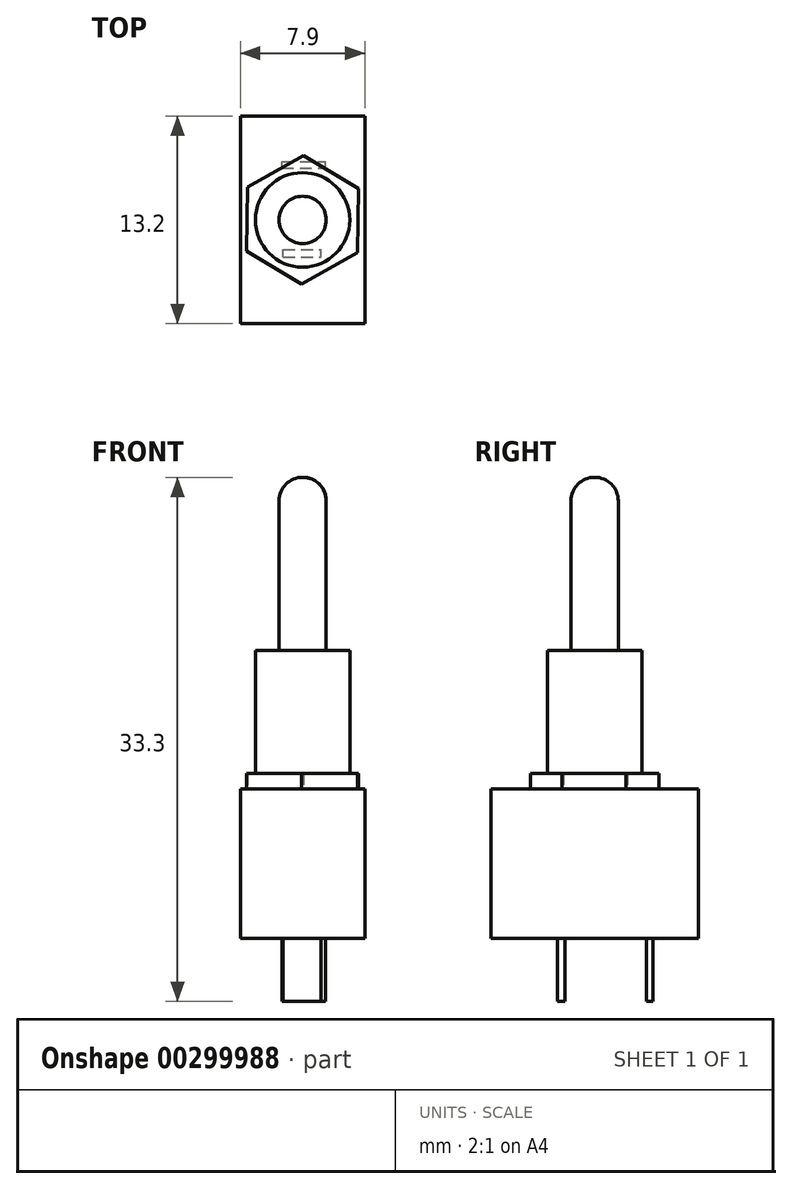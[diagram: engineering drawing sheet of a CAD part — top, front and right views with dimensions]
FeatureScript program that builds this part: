
annotation { "Feature Type Name" : "Feature", "Feature Type Description" : "" }
export const myFeature = defineFeature(function(context is Context, id is Id, definition is map)
    precondition{}
    {
        {
            var Q0;
            Q0=qCreatedBy(makeId("Right.planeOp"),FACE);
            var sketch = newSketch(context, id + "F0", { "sketchPlane" : qUnion([Q0])});
            skLineSegment(sketch, "E0.bottom", {"start": v(0, 0) * mm, "end": v(13.2, 0) * mm});
            skLineSegment(sketch, "E0.top", {"start": v(0, 9.5) * mm, "end": v(13.2, 9.5) * mm});
            skLineSegment(sketch, "E0.left", {"start": v(0, 0) * mm, "end": v(0, 9.5) * mm});
            skLineSegment(sketch, "E0.right", {"start": v(13.2, 0) * mm, "end": v(13.2, 9.5) * mm});
            skSolve(sketch);
        }
        {
            var Q0;
            Q0 = qSketchRegion(id + "F0", true);
            extrude(context, id + "F1", {"entities" : qUnion([Q0]), "depth" : 7.9 * mm});
        }
        {
            var Q0;
            Q0=makeQuery(id+"F1.opExtrude","SWEPT_FACE",FACE,{"disambiguationData":[OSD([sQuery(id+"F0.wireOp",EDGE,"E0.top")])]});
            var sketch = newSketch(context, id + "F2", { "sketchPlane" : qUnion([Q0])});
            skCircle(sketch, "E1", {"center": v(3.95, 6.6) * mm, "radius": 3 * mm});
            skPoint(sketch, "E1.centerSnap0", {"position": v(0, 6.6) * mm});
            skSolve(sketch);
        }
        {
            var Q0;
            Q0 = qSketchRegion(id + "F2", true);
            extrude(context, id + "F3", {"entities" : qUnion([Q0]), "operationType" : NewBodyOperationType.ADD, "depth" : 8.8 * mm});
        }
        {
            var Q0;
            Q0=makeQuery(id+"F3.opExtrude","CAP_FACE",FACE,{"disambiguationData":[OSD([sQuery(id+"F2.wireOp",EDGE,"E1")])],"isStart":false});
            var sketch = newSketch(context, id + "F4", { "sketchPlane" : qUnion([Q0])});
            skCircle(sketch, "E2", {"center": v(3.95, 6.6) * mm, "radius": 1.5 * mm});
            skSolve(sketch);
        }
        {
            var Q0;
            Q0 = qSketchRegion(id + "F4", true);
            extrude(context, id + "F5", {"entities" : qUnion([Q0]), "operationType" : NewBodyOperationType.ADD, "depth" : 11 * mm});
        }
        {
            var Q0;
            Q0=makeQuery(id+"F5.opExtrude","CAP_EDGE",EDGE,{"disambiguationData":[OSD([sQuery(id+"F4.wireOp",EDGE,"E2")])],"isStart":false});
            fillet(context, id + "F6", {"entities" : qUnion([Q0]), "radius" : 1.5 * mm, "tangentPropagation" : true, "allowEdgeOverflow" : false});
        }
        {
            var Q0;
            Q0=makeQuery(id+"F1.opExtrude","SWEPT_FACE",FACE,{"disambiguationData":[OSD([sQuery(id+"F0.wireOp",EDGE,"E0.bottom")])]});
            var sketch = newSketch(context, id + "F7", { "sketchPlane" : qUnion([Q0])});
            skLineSegment(sketch, "E3.bottom", {"start": v(2.7, -4.25) * mm, "end": v(5.13, -4.25) * mm});
            skLineSegment(sketch, "E3.top", {"start": v(2.7, -4.72) * mm, "end": v(5.13, -4.72) * mm});
            skLineSegment(sketch, "E3.left", {"start": v(2.7, -4.25) * mm, "end": v(2.7, -4.72) * mm});
            skLineSegment(sketch, "E3.right", {"start": v(5.13, -4.25) * mm, "end": v(5.13, -4.72) * mm});
            skLineSegment(sketch, "E4.bottom", {"start": v(2.63, -9.9) * mm, "end": v(5.42, -9.9) * mm});
            skLineSegment(sketch, "E4.top", {"start": v(2.63, -10.29) * mm, "end": v(5.42, -10.29) * mm});
            skLineSegment(sketch, "E4.left", {"start": v(2.63, -9.9) * mm, "end": v(2.63, -10.29) * mm});
            skLineSegment(sketch, "E4.right", {"start": v(5.42, -9.9) * mm, "end": v(5.42, -10.29) * mm});
            skSolve(sketch);
        }
        {
            var Q0;
            Q0 = qSketchRegion(id + "F7", true);
            extrude(context, id + "F8", {"entities" : qUnion([Q0]), "operationType" : NewBodyOperationType.ADD, "depth" : 4 * mm});
        }
        {
            var Q0;
            Q0=makeQuery(id+"F1.opExtrude","SWEPT_FACE",FACE,{"disambiguationData":[OSD([sQuery(id+"F0.wireOp",EDGE,"E0.top")])]});
            var sketch = newSketch(context, id + "F9", { "sketchPlane" : qUnion([Q0])});
            skCircle(sketch, "E5.cCircle", {"center": v(3.95, 6.6) * mm, "radius": 3.53 * mm, "construction": true});
            skLineSegment(sketch, "E5.0", {"start": v(7.45, 4.52) * mm, "end": v(3.9, 2.53) * mm});
            skLineSegment(sketch, "E5.1", {"start": v(3.9, 2.53) * mm, "end": v(0.4, 4.6) * mm});
            skLineSegment(sketch, "E5.2", {"start": v(0.4, 4.6) * mm, "end": v(0.45, 8.68) * mm});
            skLineSegment(sketch, "E5.3", {"start": v(0.45, 8.68) * mm, "end": v(4, 10.67) * mm});
            skLineSegment(sketch, "E5.4", {"start": v(4, 10.67) * mm, "end": v(7.5, 8.6) * mm});
            skLineSegment(sketch, "E5.5", {"start": v(7.5, 8.6) * mm, "end": v(7.45, 4.52) * mm});
            skPoint(sketch, "E5.0.midPoint", {"position": v(5.67, 3.52) * mm});
            skSolve(sketch);
        }
        {
            var Q0;
            Q0 = qSketchRegion(id + "F9", true);
            extrude(context, id + "F10", {"entities" : qUnion([Q0]), "operationType" : NewBodyOperationType.ADD, "depth" : 1 * mm});
        }
    });
